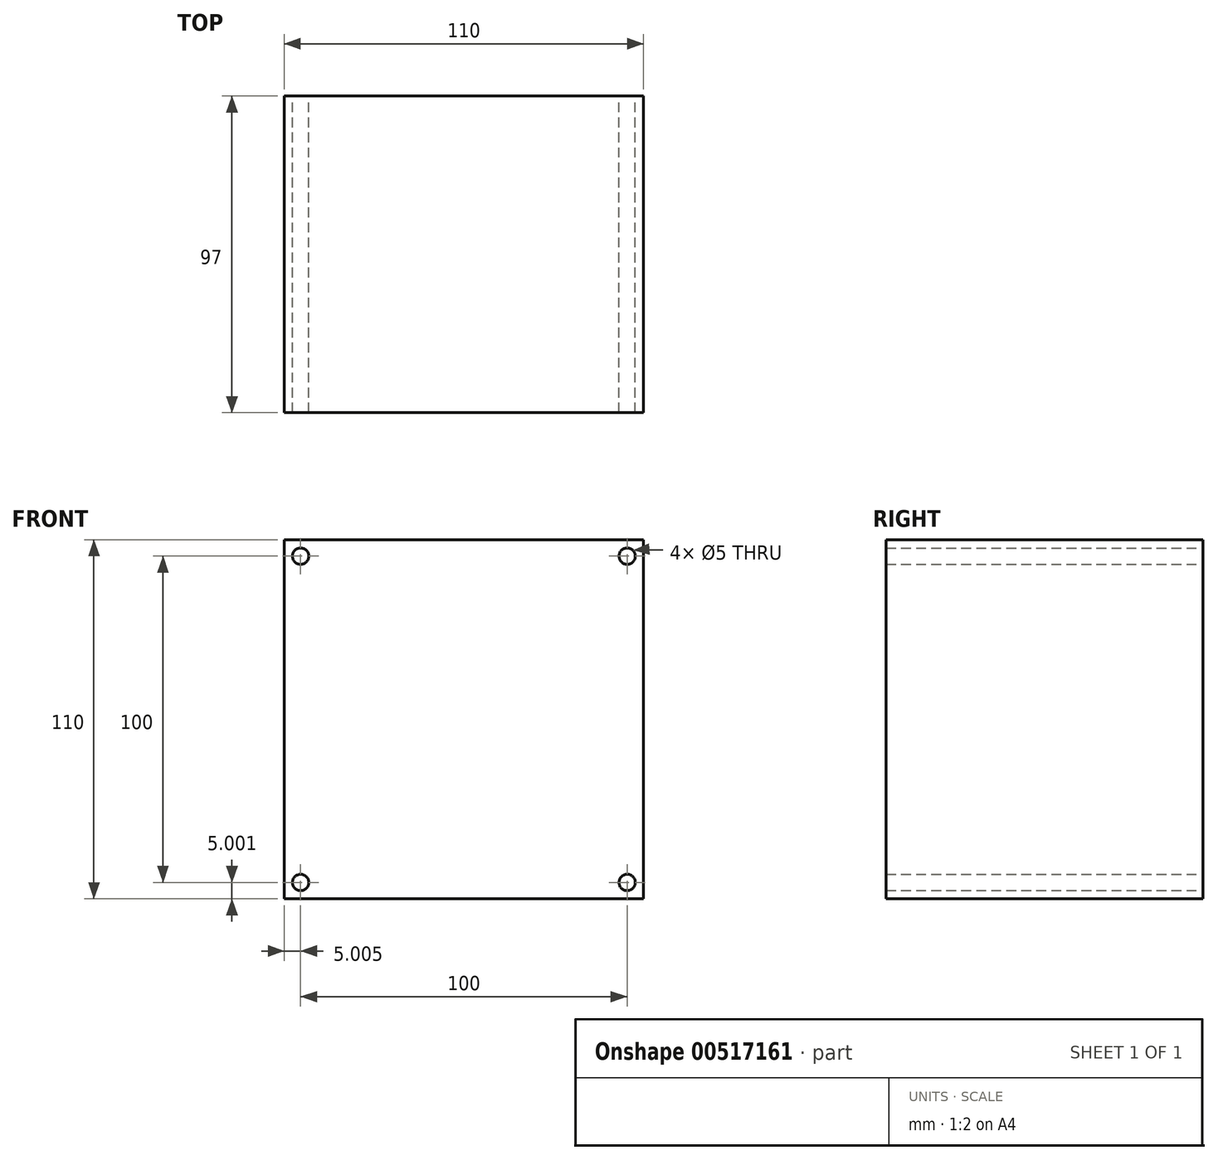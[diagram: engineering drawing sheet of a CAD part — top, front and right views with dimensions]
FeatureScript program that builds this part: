
annotation { "Feature Type Name" : "Feature", "Feature Type Description" : "" }
export const myFeature = defineFeature(function(context is Context, id is Id, definition is map)
    precondition{}
    {
        {
            var Q0;
            Q0=qCreatedBy(makeId("Front.planeOp"),FACE);
            var sketch = newSketch(context, id + "F0", { "sketchPlane" : qUnion([Q0])});
            skLineSegment(sketch, "E0.bottom", {"start": v(-69.29, -55.3) * mm, "end": v(40.71, -55.3) * mm});
            skLineSegment(sketch, "E0.top", {"start": v(-69.29, 54.7) * mm, "end": v(40.71, 54.7) * mm});
            skLineSegment(sketch, "E0.left", {"start": v(-69.29, -55.3) * mm, "end": v(-69.29, 54.7) * mm});
            skLineSegment(sketch, "E0.right", {"start": v(40.71, -55.3) * mm, "end": v(40.71, 54.7) * mm});
            skLineSegment(sketch, "E1.bottom", {"start": v(-39.29, 26.17) * mm, "end": v(10.71, 26.17) * mm, "construction": true});
            skLineSegment(sketch, "E1.top", {"start": v(-39.29, -23.83) * mm, "end": v(10.71, -23.83) * mm, "construction": true});
            skLineSegment(sketch, "E1.left", {"start": v(-39.29, 26.17) * mm, "end": v(-39.29, -23.83) * mm, "construction": true});
            skLineSegment(sketch, "E1.right", {"start": v(10.71, 26.17) * mm, "end": v(10.71, -23.83) * mm, "construction": true});
            skLineSegment(sketch, "E2", {"start": v(40.71, 0) * mm, "end": v(10.71, 0) * mm, "construction": true});
            skLineSegment(sketch, "E3", {"start": v(-39.29, -0.3) * mm, "end": v(-69.29, -0.3) * mm, "construction": true});
            skPoint(sketch, "E3.startSnap1", {"position": v(-69.29, -0.3) * mm});
            skPoint(sketch, "E4", {"position": v(10.71, 26.17) * mm});
            skPoint(sketch, "E5", {"position": v(10.71, -23.83) * mm});
            skPoint(sketch, "E6", {"position": v(-39.29, -23.83) * mm});
            skPoint(sketch, "E7", {"position": v(-39.29, 26.17) * mm});
            skSolve(sketch);
        }
        {
            var Q0;
            Q0=makeQuery(id+"F0.imprint","IMPRINT",FACE,{"disambiguationData":[TD([[makeQuery(id+"F0.imprint","IMPRINT",EDGE,{"derivedFrom":sQuery(id+"F0.wireOp",EDGE,"E0.bottom")}),1.0]])]});
            extrude(context, id + "F1", {"entities" : qUnion([Q0]), "depth" : 97 * mm, "offsetDistance" : 25 * mm});
        }
        {
            var Q0;
            Q0=makeQuery(id+"F1.opExtrude","CAP_FACE",FACE,{"disambiguationData":[OSD([sQuery(id+"F0.wireOp",EDGE,"E0.bottom"),sQuery(id+"F0.wireOp",EDGE,"E0.top"),sQuery(id+"F0.wireOp",EDGE,"E0.left"),sQuery(id+"F0.wireOp",EDGE,"E0.right")])],"isStart":true});
            var sketch = newSketch(context, id + "F2", { "sketchPlane" : qUnion([Q0])});
            skLineSegment(sketch, "E8.bottom", {"start": v(-35.71, 49.7) * mm, "end": v(64.29, 49.7) * mm, "construction": true});
            skLineSegment(sketch, "E8.top", {"start": v(-35.71, -50.3) * mm, "end": v(64.29, -50.3) * mm, "construction": true});
            skLineSegment(sketch, "E8.left", {"start": v(-35.71, 49.7) * mm, "end": v(-35.71, -50.3) * mm, "construction": true});
            skLineSegment(sketch, "E8.right", {"start": v(64.29, 49.7) * mm, "end": v(64.29, -50.3) * mm, "construction": true});
            skPoint(sketch, "E9", {"position": v(-35.71, 49.7) * mm});
            skPoint(sketch, "E10", {"position": v(64.29, 49.7) * mm});
            skPoint(sketch, "E11", {"position": v(64.29, -50.3) * mm});
            skPoint(sketch, "E12", {"position": v(-35.71, -50.3) * mm});
            skLineSegment(sketch, "E13", {"start": v(-40.71, 54.7) * mm, "end": v(69.29, -55.3) * mm, "construction": true});
            skLineSegment(sketch, "E14", {"start": v(11.07, 54.7) * mm, "end": v(11.07, 49.7) * mm, "construction": true});
            skLineSegment(sketch, "E15", {"start": v(14.29, -50.3) * mm, "end": v(14.29, -55.3) * mm, "construction": true});
            skSolve(sketch);
        }
        {
            var Q0;
            Q0=sQuery(id+"F2.wireOp",VERTEX,"E9");
            var Q1;
            Q1=sQuery(id+"F2.wireOp",VERTEX,"E12");
            var Q2;
            Q2=sQuery(id+"F2.wireOp",VERTEX,"E11");
            var Q3;
            Q3=sQuery(id+"F2.wireOp",VERTEX,"E10");
            var Q4;
            Q4=makeQuery(id+"F1.opExtrude","SWEPT_BODY",BODY,{"disambiguationData":[OSD([sQuery(id+"F0.wireOp",EDGE,"E0.bottom"),sQuery(id+"F0.wireOp",EDGE,"E0.top"),sQuery(id+"F0.wireOp",EDGE,"E0.left"),sQuery(id+"F0.wireOp",EDGE,"E0.right")])]});
            hole(context, id + "F3", {"style" : HoleStyle.SIMPLE, "endStyle" : HoleEndStyle.THROUGH, "holeDiameter" : 5 * mm, "isTappedThrough" : true, "tappedDepth" : 12 * mm, "tapClearance" : 3, "locations" : qUnion([Q0, Q1, Q2, Q3]), "scope" : qUnion([Q4])});
        }
    });
